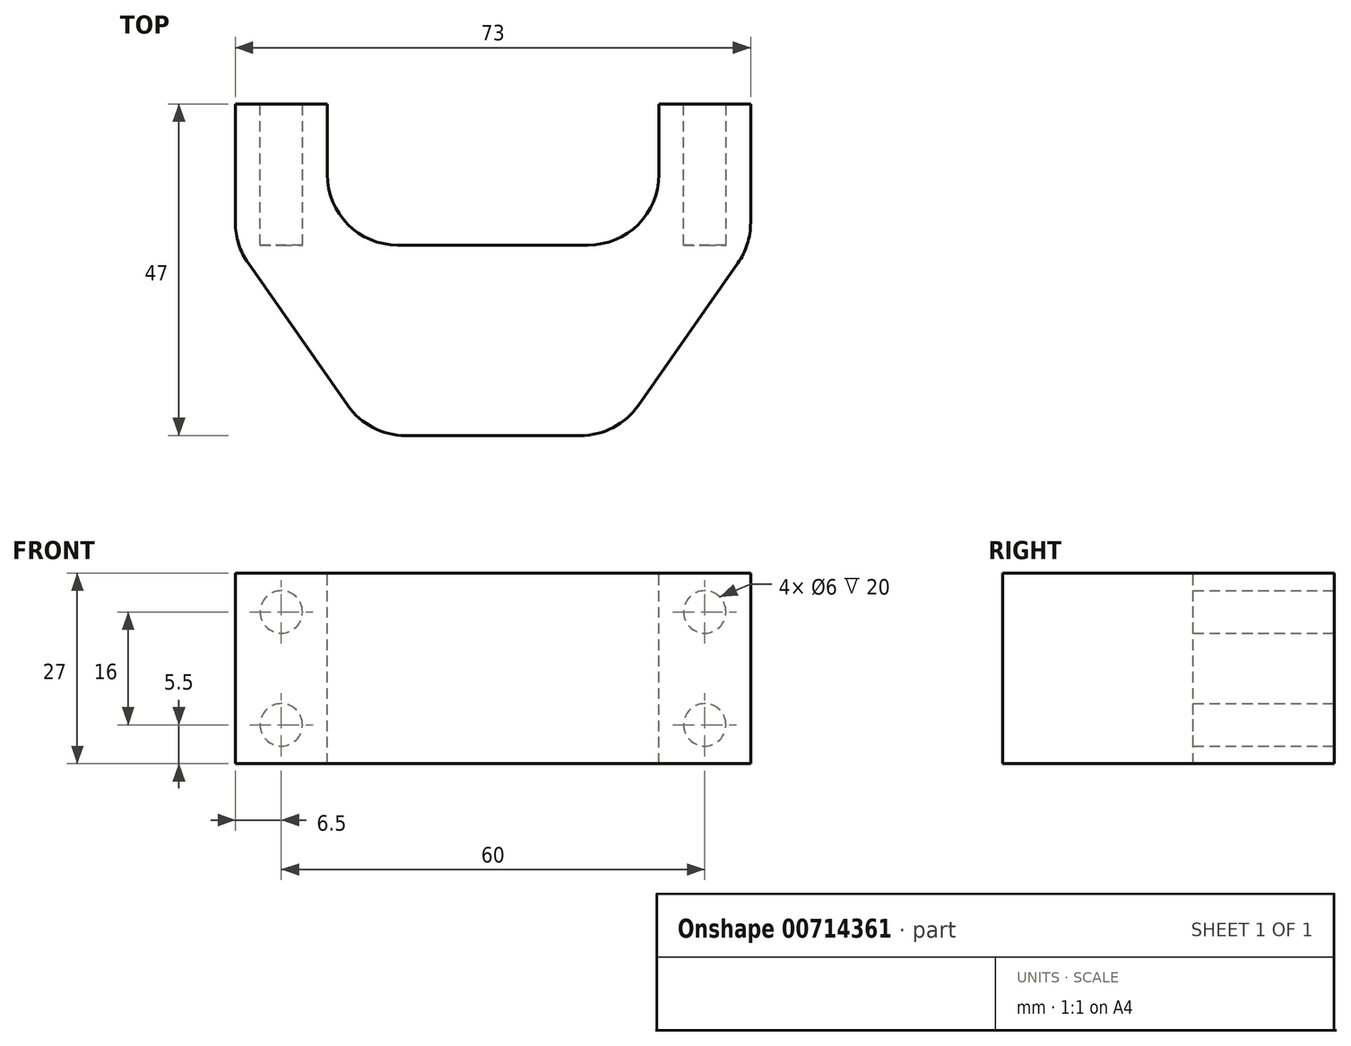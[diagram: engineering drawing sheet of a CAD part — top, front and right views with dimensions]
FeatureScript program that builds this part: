
annotation { "Feature Type Name" : "Feature", "Feature Type Description" : "" }
export const myFeature = defineFeature(function(context is Context, id is Id, definition is map)
    precondition{}
    {
        {
            var Q0;
            Q0=qCreatedBy(makeId("Front.planeOp"),FACE);
            var sketch = newSketch(context, id + "F0", { "sketchPlane" : qUnion([Q0])});
            skCircle(sketch, "E0", {"center": v(-30, -8) * mm, "radius": 3 * mm});
            skCircle(sketch, "E1.0.1.0", {"center": v(-30, 8) * mm, "radius": 3 * mm});
            skCircle(sketch, "E1.1.0.0", {"center": v(30, -8) * mm, "radius": 3 * mm});
            skCircle(sketch, "E1.1.1.0", {"center": v(30, 8) * mm, "radius": 3 * mm});
            skLineSegment(sketch, "E1.direction1", {"start": v(-30, -8) * mm, "end": v(30, -8) * mm, "construction": true});
            skLineSegment(sketch, "E1.direction2", {"start": v(-30, -8) * mm, "end": v(-30, 8) * mm, "construction": true});
            skLineSegment(sketch, "E2.bottom", {"start": v(-23.5, -13.5) * mm, "end": v(-36.5, -13.5) * mm});
            skLineSegment(sketch, "E2.top", {"start": v(-23.5, 13.5) * mm, "end": v(-36.5, 13.5) * mm});
            skLineSegment(sketch, "E2.left", {"start": v(-23.5, -13.5) * mm, "end": v(-23.5, 13.5) * mm});
            skLineSegment(sketch, "E2.right", {"start": v(-36.5, -13.5) * mm, "end": v(-36.5, 13.5) * mm});
            skPoint(sketch, "E2.middle", {"position": v(-30, 0) * mm});
            skLineSegment(sketch, "E3.MirrorCS", {"start": v(23.5, 13.5) * mm, "end": v(36.5, 13.5) * mm});
            skLineSegment(sketch, "E4.MirrorCS", {"start": v(23.5, -13.5) * mm, "end": v(23.5, 13.5) * mm});
            skLineSegment(sketch, "E5.MirrorCS", {"start": v(23.5, -13.5) * mm, "end": v(36.5, -13.5) * mm});
            skLineSegment(sketch, "E6.MirrorCS", {"start": v(36.5, -13.5) * mm, "end": v(36.5, 13.5) * mm});
            skSolve(sketch);
        }
        {
            var Q0;
            Q0=makeQuery(id+"F0.imprint","IMPRINT",FACE,{"disambiguationData":[TD([[makeQuery(id+"F0.imprint","IMPRINT",EDGE,{"derivedFrom":sQuery(id+"F0.wireOp",EDGE,"E0")}),-1.0]])]});
            var Q1;
            Q1=makeQuery(id+"F0.imprint","IMPRINT",FACE,{"disambiguationData":[TD([[makeQuery(id+"F0.imprint","IMPRINT",EDGE,{"derivedFrom":sQuery(id+"F0.wireOp",EDGE,"E1.1.0.0")}),-1.0]])]});
            extrude(context, id + "F1", {"entities" : qUnion([Q0, Q1]), "depth" : 20 * mm, "offsetDistance" : 25 * mm});
        }
        {
            var Q0;
            Q0=qCreatedBy(makeId("Top.planeOp"),FACE);
            var sketch = newSketch(context, id + "F2", { "sketchPlane" : qUnion([Q0])});
            skPoint(sketch, "E7.0", {"position": v(-36.5, -20) * mm});
            skPoint(sketch, "E8.0", {"position": v(36.5, -20) * mm});
            skLineSegment(sketch, "E9", {"start": v(-36.5, -20) * mm, "end": v(-17.6, -47) * mm});
            skLineSegment(sketch, "E10", {"start": v(-17.6, -47) * mm, "end": v(17.6, -47) * mm});
            skLineSegment(sketch, "E11", {"start": v(17.6, -47) * mm, "end": v(36.5, -20) * mm});
            skLineSegment(sketch, "E12", {"start": v(36.5, -20) * mm, "end": v(-36.5, -20) * mm});
            skSolve(sketch);
        }
        {
            var Q0;
            Q0=makeQuery(id+"F2.imprint","IMPRINT",FACE,{"disambiguationData":[TD([[makeQuery(id+"F2.imprint","IMPRINT",EDGE,{"derivedFrom":sQuery(id+"F2.wireOp",EDGE,"E9")}),1.0]])]});
            extrude(context, id + "F3", {"entities" : qUnion([Q0]), "operationType" : NewBodyOperationType.ADD, "endBound" : BoundingType.SYMMETRIC, "depth" : 27 * mm, "offsetDistance" : 25 * mm});
        }
        {
            var Q0;
            Q0=makeQuery(id+"F1.opExtrude","CAP_EDGE",EDGE,{"disambiguationData":[OSD([sQuery(id+"F0.wireOp",EDGE,"E2.left")])],"isStart":false});
            var Q1;
            Q1=makeQuery(id+"F1.opExtrude","CAP_EDGE",EDGE,{"disambiguationData":[OSD([sQuery(id+"F0.wireOp",EDGE,"E4.MirrorCS")])],"isStart":false});
            var Q2;
            Q2=makeQuery(id+"F3.opExtrude","SWEPT_EDGE",EDGE,{"disambiguationData":[OSD([sQuery(id+"F2.wireOp",EDGE,"E9"),sQuery(id+"F2.wireOp",EDGE,"E10")])]});
            var Q3;
            Q3=makeQuery(id+"F3.opExtrude","SWEPT_EDGE",EDGE,{"disambiguationData":[OSD([sQuery(id+"F2.wireOp",EDGE,"E10"),sQuery(id+"F2.wireOp",EDGE,"E11")])]});
            var Q4;
            Q4=makeQuery(id+"F3.boolean.opBoolean","MERGE",EDGE,{"derivedFrom":[makeQuery(id+"F1.opExtrude","CAP_EDGE",EDGE,{"disambiguationData":[OSD([sQuery(id+"F0.wireOp",EDGE,"E2.right")])],"isStart":false}),makeQuery(id+"F3.opExtrude","SWEPT_EDGE",EDGE,{"disambiguationData":[OSD([sQuery(id+"F2.wireOp",EDGE,"E9"),sQuery(id+"F2.wireOp",EDGE,"E12")])]})]});
            var Q5;
            Q5=makeQuery(id+"F3.boolean.opBoolean","MERGE",EDGE,{"derivedFrom":[makeQuery(id+"F1.opExtrude","CAP_EDGE",EDGE,{"disambiguationData":[OSD([sQuery(id+"F0.wireOp",EDGE,"E6.MirrorCS")])],"isStart":false}),makeQuery(id+"F3.opExtrude","SWEPT_EDGE",EDGE,{"disambiguationData":[OSD([sQuery(id+"F2.wireOp",EDGE,"E11"),sQuery(id+"F2.wireOp",EDGE,"E12")])]})]});
            fillet(context, id + "F4", {"entities" : qUnion([Q0, Q1, Q2, Q3, Q4, Q5]), "radius" : 10 * mm, "tangentPropagation" : true, "allowEdgeOverflow" : false});
        }
    });
